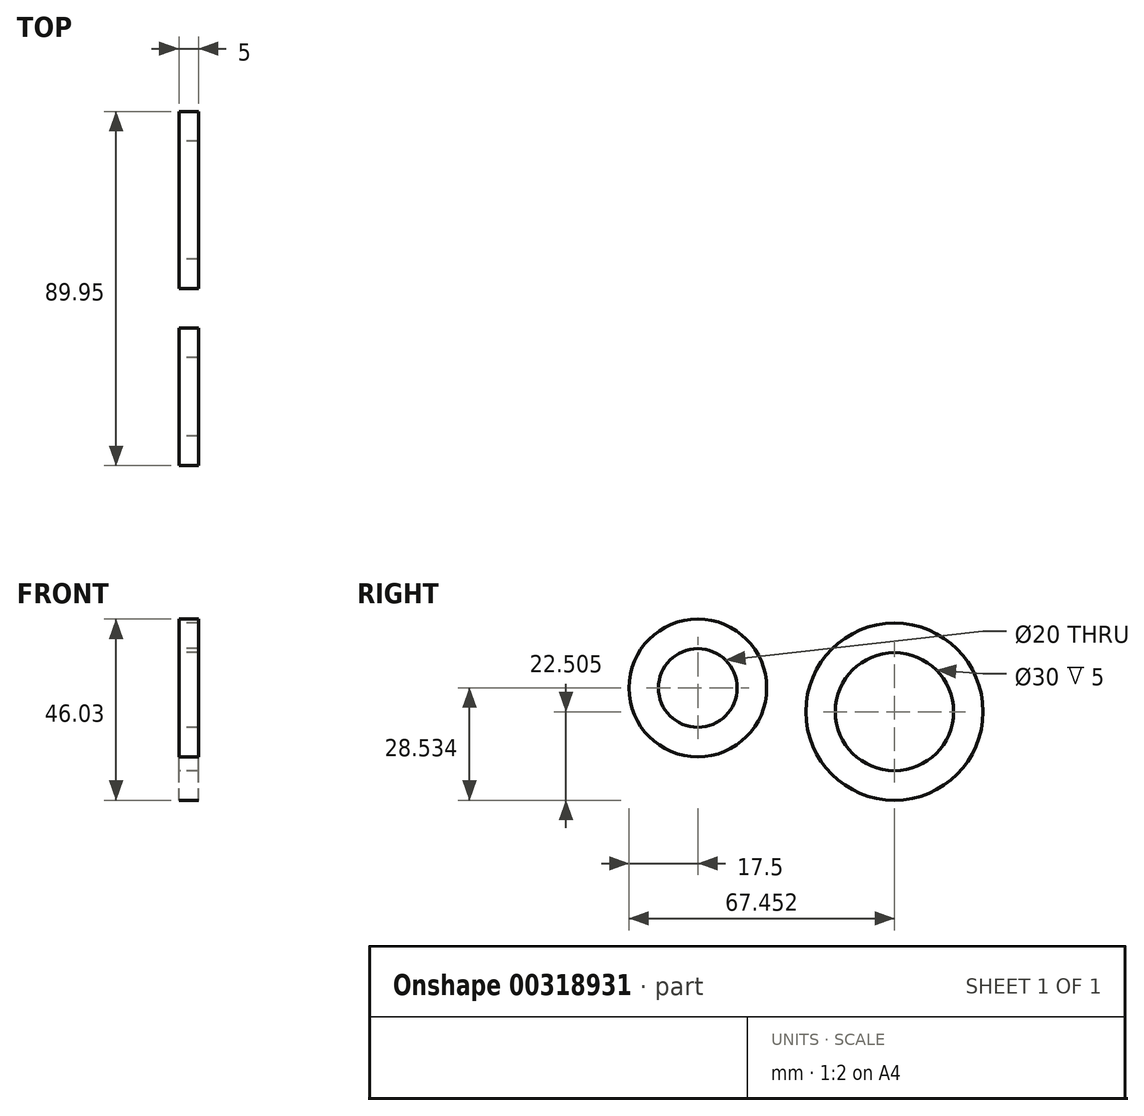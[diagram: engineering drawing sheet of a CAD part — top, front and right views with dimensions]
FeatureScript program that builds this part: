
annotation { "Feature Type Name" : "Feature", "Feature Type Description" : "" }
export const myFeature = defineFeature(function(context is Context, id is Id, definition is map)
    precondition{}
    {
        {
            var Q0;
            Q0=qCreatedBy(makeId("Right.planeOp"),FACE);
            var sketch = newSketch(context, id + "F0", { "sketchPlane" : qUnion([Q0])});
            skCircle(sketch, "E0", {"center": v(-20, 4.33) * mm, "radius": 10 * mm});
            skCircle(sketch, "E1", {"center": v(29.95, -1.7) * mm, "radius": 15 * mm});
            skCircle(sketch, "E2", {"center": v(-20, 4.33) * mm, "radius": 17.5 * mm});
            skCircle(sketch, "E3", {"center": v(29.95, -1.7) * mm, "radius": 22.5 * mm});
            skSolve(sketch);
        }
        {
            var Q0;
            Q0 = qSketchRegion(id + "F0", true);
            extrude(context, id + "F1", {"entities" : qUnion([Q0]), "depth" : 5 * mm, "offsetDistance" : 25 * mm});
        }
    });
